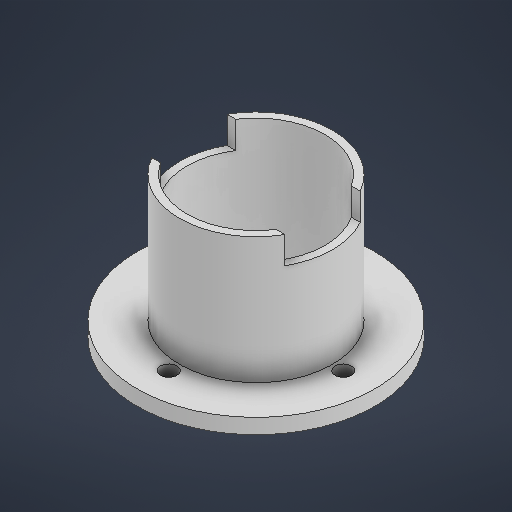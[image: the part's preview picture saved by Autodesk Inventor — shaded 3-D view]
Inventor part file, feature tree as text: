
AUTODESK INVENTOR PART (.ipt)
format: ipt  version: 2025 (Build 290162000, 162)  size: 232,960 bytes
history: native  units: in
note: dims shown in document units (in); Inventor stores cm internally (conversion verified against a paired STEP export)
features: extrude x3, sketch x2
ambient origin geometry x8: Origin, YZ Plane, XZ Plane, XY Plane, X Axis, Y Axis, Z Axis, Center Point
bodies: Solid1 (feature_tree)
feature tree (5):
  sketch  "Sketch1"  dims[d0=1.8031in d1=3.1102in]
  extrude  "Extrusion1"  Depth=3.1102in
  extrude  "Extrusion2"  Depth=1.4961in
  extrude  "Extrusion3"  Depth=1.4961in TaperAngle=360.0deg
  sketch  "Sketch Circular Pattern1"  dims[d2=2.2835in d3=0.2165in d4=1.5748in d6=360.0deg d8=0.1969in d9=0.0in d10=0.9843in d11=1.8504in d12=0.0in d13=1.4961in d14=0.0in]
